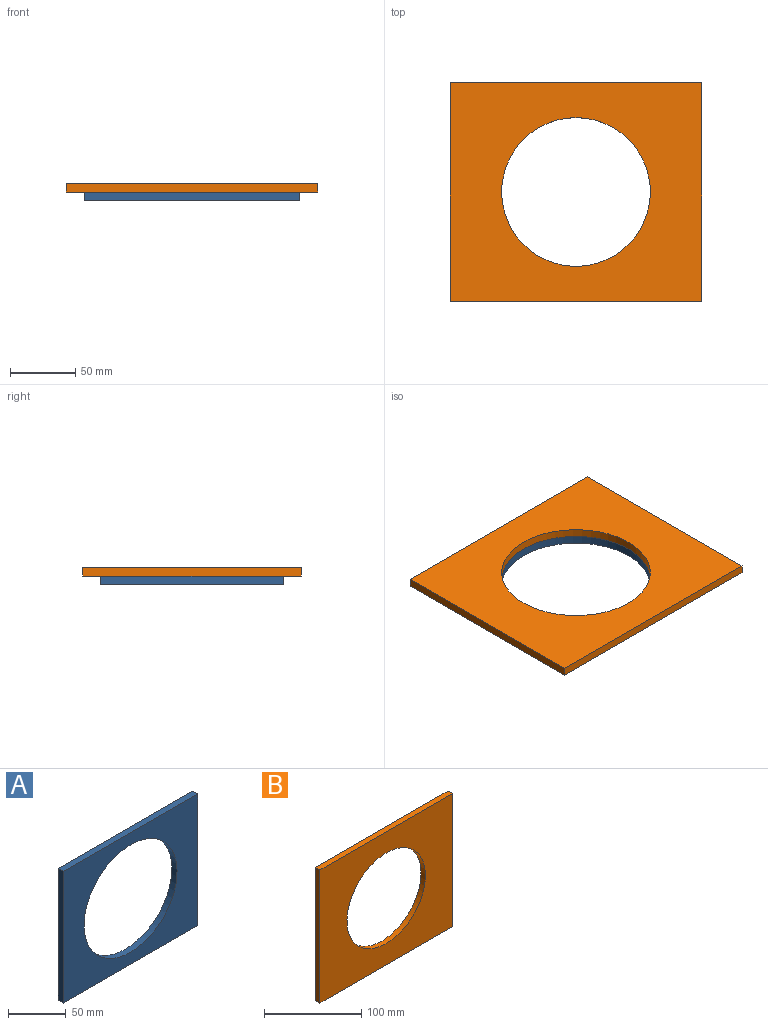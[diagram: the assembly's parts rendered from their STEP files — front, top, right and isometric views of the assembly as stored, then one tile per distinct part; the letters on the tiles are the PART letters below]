
ASSEMBLY  parts=2 mates=1
PART A: 7 faces, bbox 165x6.4x140 mm
  f0: plane 165x6.35mm, normal (0,0,1), area 1047.8mm2, adj f1,f3,f4,f5
  f1: plane 140x6.35mm, normal (-1,0,0), area 889mm2, adj f0,f2,f4,f5
  f2: plane 165x6.35mm, normal (0,0,-1), area 1047.8mm2, adj f1,f3,f4,f5
  f3: plane 140x6.35mm, normal (1,0,0), area 889mm2, adj f0,f2,f4,f5
  f4: plane 165x140mm, normal (0,-1,0), area 12839.2mm2, adj f0,f1,f2,f3,f6
  f5: plane 165x140mm, normal (0,1,0), area 12839.2mm2, adj f0,f1,f2,f3,f6
  f6: cylinder r=57.15mm len=114.3mm, axis (0,-1,0), area 2280.2mm2, adj f4,f5
PART B: 7 faces, bbox 193x6.4x168 mm
  f0: plane 193x6.35mm, normal (0,0,1), area 1225.5mm2, adj f1,f3,f4,f5
  f1: plane 168x6.35mm, normal (-1,0,0), area 1066.8mm2, adj f0,f2,f4,f5
  f2: plane 193x6.35mm, normal (0,0,-1), area 1225.5mm2, adj f1,f3,f4,f5
  f3: plane 168x6.35mm, normal (1,0,0), area 1066.8mm2, adj f0,f2,f4,f5
  f4: plane 193x168mm, normal (0,-1,0), area 22163.2mm2, adj f0,f1,f2,f3,f6
  f5: plane 193x168mm, normal (0,1,0), area 22163.2mm2, adj f0,f1,f2,f3,f6
  f6: cylinder r=57.15mm len=114.3mm, axis (0,-1,0), area 2280.2mm2, adj f4,f5
PLACE A rot(axis=(1,0,0),90deg) t=(32.05,62.82,69.68)mm
PLACE B rot(axis=(1,0,0),90deg) t=(32.05,62.82,76.03)mm fixed
MATE fastened B.f6 <-> A.f6  axis (0,0,-1) through (32.05,62.82,69.68)mm
